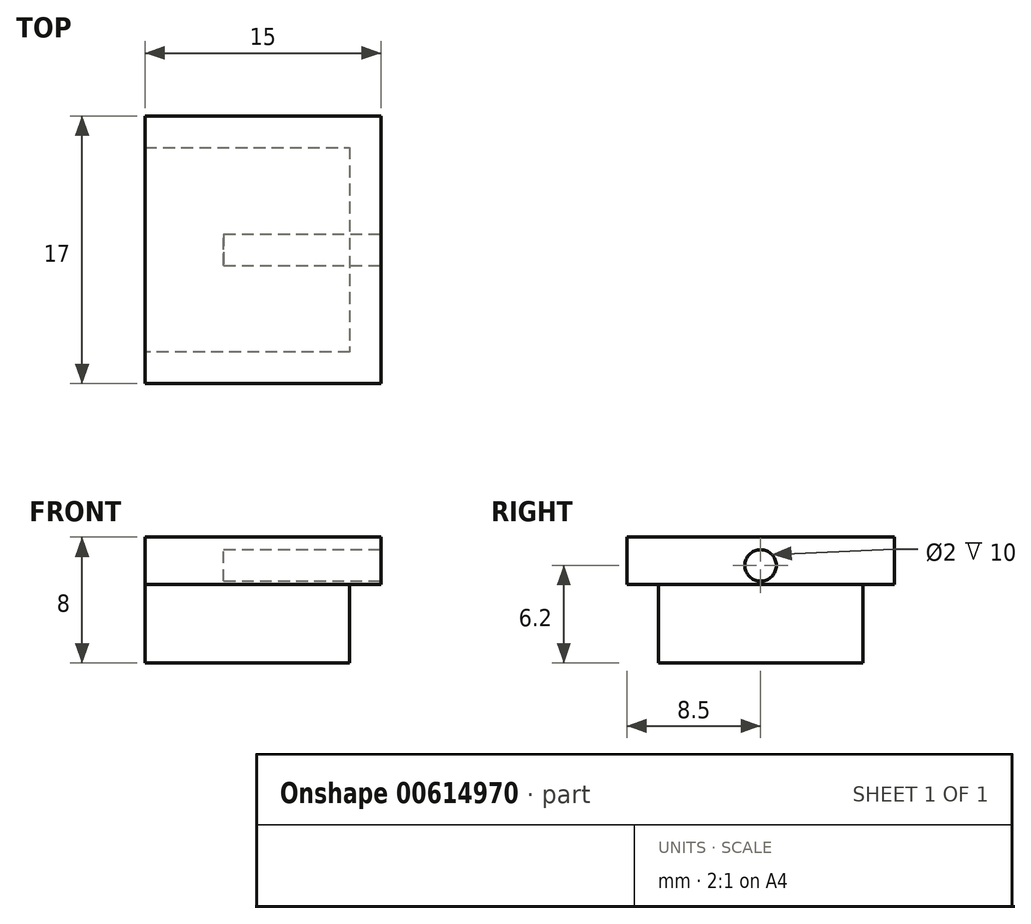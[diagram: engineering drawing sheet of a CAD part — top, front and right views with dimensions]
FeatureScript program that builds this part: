
annotation { "Feature Type Name" : "Feature", "Feature Type Description" : "" }
export const myFeature = defineFeature(function(context is Context, id is Id, definition is map)
    precondition{}
    {
        {
            var Q0;
            Q0=qCreatedBy(makeId("Top.planeOp"),FACE);
            var sketch = newSketch(context, id + "F0", { "sketchPlane" : qUnion([Q0])});
            skLineSegment(sketch, "E0", {"start": v(0, 0) * mm, "end": v(0, 13) * mm});
            skLineSegment(sketch, "E1", {"start": v(0, 13) * mm, "end": v(13, 13) * mm});
            skLineSegment(sketch, "E2", {"start": v(13, 13) * mm, "end": v(13, 0) * mm});
            skLineSegment(sketch, "E3", {"start": v(13, 0) * mm, "end": v(0, 0) * mm});
            skSolve(sketch);
        }
        {
            var Q0;
            Q0=makeQuery(id+"F0.imprint","IMPRINT",FACE,{"disambiguationData":[TD([[makeQuery(id+"F0.imprint","IMPRINT",EDGE,{"derivedFrom":sQuery(id+"F0.wireOp",EDGE,"E0")}),-1.0]])]});
            extrude(context, id + "F1", {"entities" : qUnion([Q0]), "depth" : 8 * mm, "offsetDistance" : 25 * mm});
        }
        {
            var Q0;
            Q0=makeQuery(id+"F1.opExtrude","CAP_FACE",FACE,{"disambiguationData":[OSD([sQuery(id+"F0.wireOp",EDGE,"E0"),sQuery(id+"F0.wireOp",EDGE,"E1"),sQuery(id+"F0.wireOp",EDGE,"E2"),sQuery(id+"F0.wireOp",EDGE,"E3")])],"isStart":false});
            var sketch = newSketch(context, id + "F2", { "sketchPlane" : qUnion([Q0])});
            skLineSegment(sketch, "E4", {"start": v(0, 0) * mm, "end": v(0, 0) * mm});
            skLineSegment(sketch, "E5", {"start": v(0, 0) * mm, "end": v(0, -2) * mm});
            skLineSegment(sketch, "E6", {"start": v(0, -2) * mm, "end": v(15, -2) * mm});
            skLineSegment(sketch, "E7", {"start": v(15, -2) * mm, "end": v(15, 15) * mm});
            skLineSegment(sketch, "E8", {"start": v(15, 15) * mm, "end": v(0, 15) * mm});
            skLineSegment(sketch, "E9", {"start": v(0, 15) * mm, "end": v(0, -2) * mm});
            skSolve(sketch);
        }
        {
            var Q0;
            {var subQ3=sQuery(id+"F2.wireOp",EDGE,"E6");Q0=makeQuery(id+"F2.imprint","IMPRINT",FACE,{"disambiguationData":[TD([[makeQuery(id+"F2.imprint","IMPRINT",EDGE,{"derivedFrom":subQ3}),1.0]])]});}
            extrude(context, id + "F3", {"entities" : qUnion([Q0]), "operationType" : NewBodyOperationType.ADD, "oppositeDirection" : true, "depth" : 3 * mm, "offsetDistance" : 25 * mm});
        }
        {
            var Q0;
            Q0=makeQuery(id+"F3.opExtrude","SWEPT_FACE",FACE,{"disambiguationData":[OSD([sQuery(id+"F2.wireOp",EDGE,"E7")])]});
            var sketch = newSketch(context, id + "F4", { "sketchPlane" : qUnion([Q0])});
            skLineSegment(sketch, "E10", {"start": v(15, 8) * mm, "end": v(6.5, 8) * mm});
            skLineSegment(sketch, "E11", {"start": v(6.5, 8) * mm, "end": v(6.5, 6.2) * mm});
            skCircle(sketch, "E12", {"center": v(6.5, 6.2) * mm, "radius": 1 * mm});
            skSolve(sketch);
        }
        {
            var Q0;
            Q0=makeQuery(id+"F4.imprint","IMPRINT",FACE,{"disambiguationData":[TD([[makeQuery(id+"F4.imprint","IMPRINT",EDGE,{"derivedFrom":sQuery(id+"F4.wireOp",EDGE,"E12")}),1.0]])]});
            extrude(context, id + "F5", {"entities" : qUnion([Q0]), "operationType" : NewBodyOperationType.REMOVE, "oppositeDirection" : true, "depth" : 10 * mm, "offsetDistance" : 25 * mm});
        }
    });
